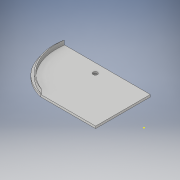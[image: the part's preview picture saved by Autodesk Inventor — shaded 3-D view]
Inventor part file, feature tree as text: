
AUTODESK INVENTOR PART (.ipt)
format: ipt  version: 2019 (Build 230136000, 136)  size: 115,200 bytes
history: native  units: mm
features: sketch x5, extrude x2, hole x1
ambient origin geometry x8: Origin, YZ Plane, XZ Plane, XY Plane, X Axis, Y Axis, Z Axis, Center Point
bodies: Solid1 (feature_tree)
feature tree (8):
  sketch  "Sketch1"  dims[d0=400.0mm d1=250.0mm]
  sketch  "Sketch2"  dims[d2=250.0mm d3=10.0mm d4=0.0mm]
  sketch  "Sketch3"  dims[d5=20.0mm d6=6.0mm d7=4.0mm d8=2.0mm d9=90.0deg d10=8.0mm d11=20.594885mm d12=20.0mm d13=0.0mm]
  extrude  "Extrusion1"  Depth=250.0mm
  hole  "Hole1"  [1 undecoded]
  extrude  "Extrusion2"  Depth=20.0mm TaperAngle=0.0deg
  sketch  "Sketch4"
  sketch  "Sketch5"
note: 1 required parameter value undecoded (feature->parameter linkage not recoverable at this tier; creation-order binding heuristic only, values carry confidence <= 0.55)
